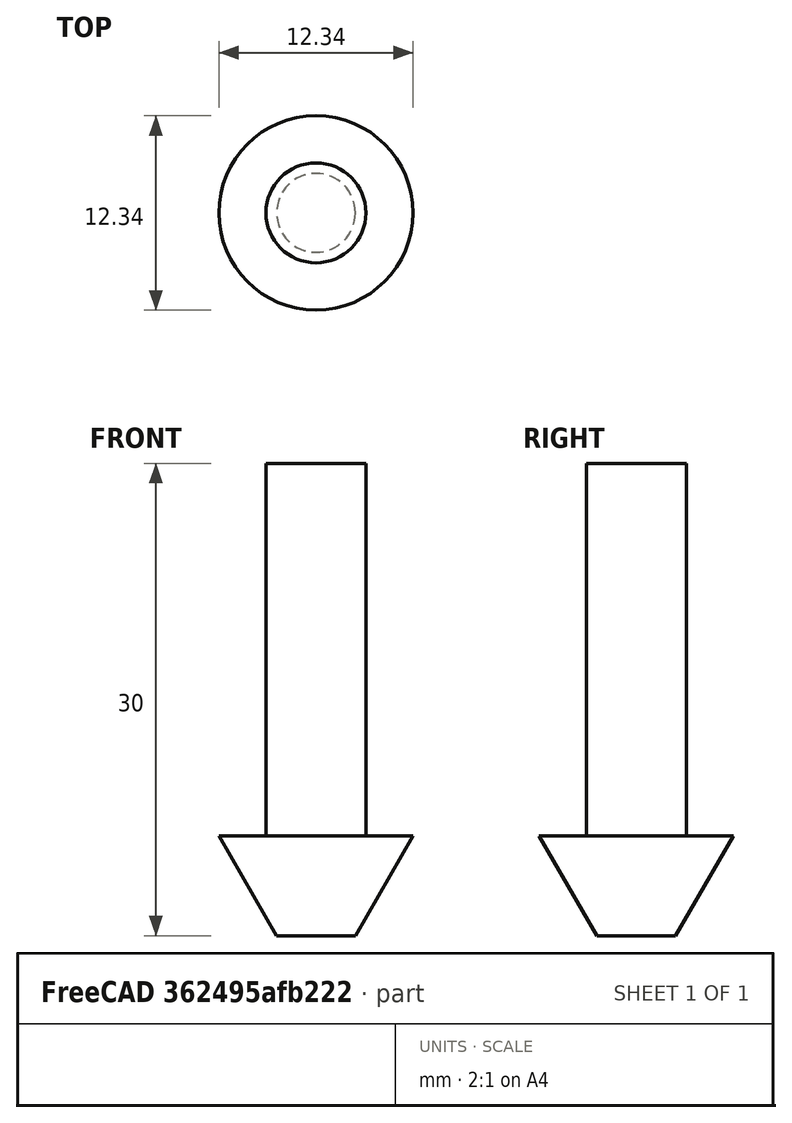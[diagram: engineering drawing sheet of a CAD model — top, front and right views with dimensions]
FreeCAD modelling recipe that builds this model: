
FCSTD DOCUMENT  (FreeCAD 0.21R32331 +3 (Git))
Label: chamfer
License: Creative Commons Attribution 4.0
LicenseURL: https://creativecommons.org/licenses/by/4.0/
objects: Sketcher::SketchObject×1, PartDesign::Revolution×1, App::FeaturePython×1, PartDesign::Body×1
note: 4 computed .brp shape members not serialized (recipe doc carries the construction recipe); baked Part::Feature solids carry a one-line shape summary decoded from their .brp

FEATURE [Sketcher::SketchObject] Sketch
  FullyConstrained = true
  MapMode = 5
  Placement = pos=(0,0,0) rot=(1,0,0;1.5708rad)
  Support = -> [XZ_Plane]
  expr: Constraints[10] = <<Attributes>>.CuttingEdgeHeight
  expr: Constraints[13] = <<Attributes>>.ShankDiameter / 2
  expr: Constraints[14] = <<Attributes>>.TipDiameter / 2 + 1 um
  expr: Constraints[16] = <<Attributes>>.CuttingEdgeAngle / 2
  expr: Constraints[5] = <<Attributes>>.Length
  sketch-geometry (6):
    g0: LineSegment StartX=0 StartY=30 StartZ=0 EndX=0 EndY=0 EndZ=0
    g1: LineSegment StartX=0 StartY=0 StartZ=0 EndX=2.501 EndY=0 EndZ=0
    g2: LineSegment StartX=2.501 StartY=0 StartZ=0 EndX=6.16717 EndY=6.35 EndZ=0
    g3: LineSegment StartX=3.175 StartY=30 StartZ=0 EndX=0 EndY=30 EndZ=0
    g4: LineSegment StartX=3.175 StartY=6.36 StartZ=0 EndX=6.16717 EndY=6.35 EndZ=0
    g5: LineSegment StartX=3.175 StartY=30 StartZ=0 EndX=3.175 EndY=6.36 EndZ=0
  constraints (17):
    c: Vertical(g0)
    c: Coincident(g0,g1)
    c: Horizontal(g1)
    c: Coincident(g1,g2)
    c: Horizontal(g3)
    c: DistanceY(g2,g3) = 30
    c: Coincident(g2,g4)
    c: Vertical(g5)
    c: Coincident(g3,g5)
    c: Coincident(g4,g5)
    c: DistanceY(g2) = 6.35
    c: Coincident(g0,g-1)
    c: Coincident(g0,g3)
    c: DistanceX(g-2,g3) = 3.175
    c: DistanceX(g-2,g1) = 2.501
    c: DistanceY(g2,g4) = 0.01
    c: Angle(g2,g-2) = 0.523599
FEATURE [PartDesign::Revolution] Revolution
  AllowMultiFace = false
  Angle = 360
  Axis = (0,-2e-16,1)
  Base = (0,0,0)
  Placement = pos=(0,0,0) rot=(1,0,0;1.5708rad)
  Profile = -> Sketch
  ReferenceAxis = -> Sketch [V_Axis]
  Reversed = true
FEATURE [App::FeaturePython] PropertyBag  label="Attributes"  # WARN: FeaturePython — macro-defined, semantics opaque (R4)
  Chipload = 0
  CustomPropertyGroups = Attributes | Shape
  CuttingEdgeAngle = 60
  CuttingEdgeHeight = 6.35
  Diameter = 12
  Flutes = 0
  Length = 30
  Material = 0
  ShankDiameter = 6.35
  TipDiameter = 5
FEATURE [PartDesign::Body] Body  label="ChamferTool"
  Group = -> [Sketch,Revolution,PropertyBag]
  Origin = -> Origin
  Tip = -> Revolution
